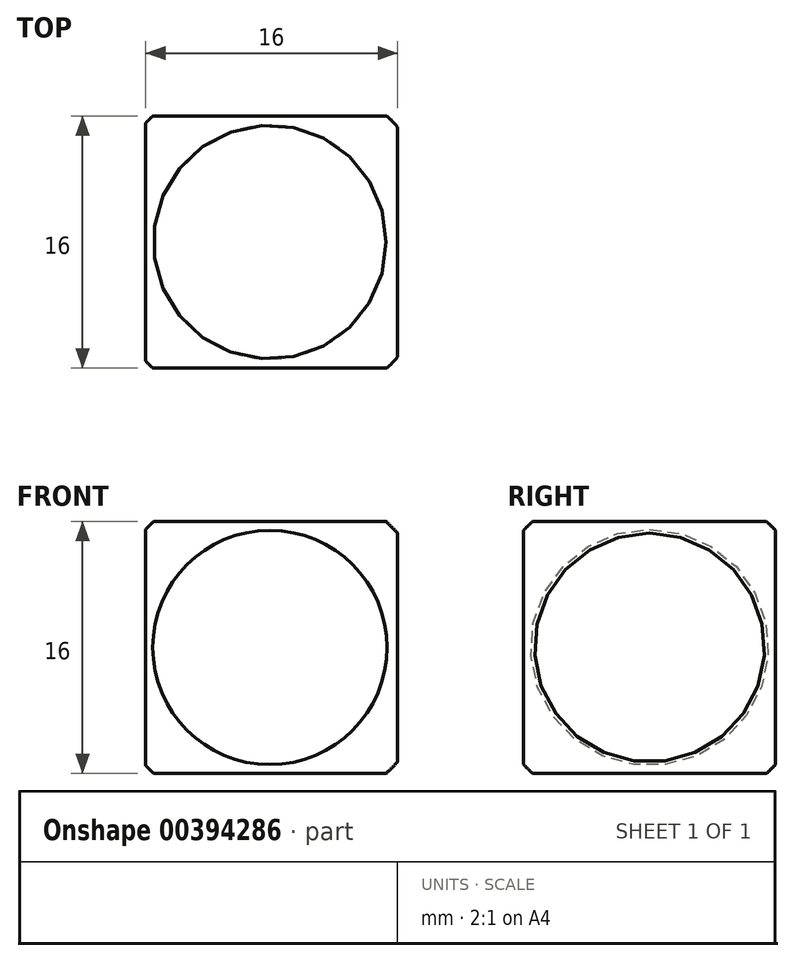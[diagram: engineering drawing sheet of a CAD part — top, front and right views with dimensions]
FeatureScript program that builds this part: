
annotation { "Feature Type Name" : "Feature", "Feature Type Description" : "" }
export const myFeature = defineFeature(function(context is Context, id is Id, definition is map)
    precondition{}
    {
        {
            var Q0;
            Q0=qCreatedBy(makeId("Top.planeOp"),FACE);
            var sketch = newSketch(context, id + "F0", { "sketchPlane" : qUnion([Q0])});
            skLineSegment(sketch, "E0.bottom", {"start": v(8, -8) * mm, "end": v(-8, -8) * mm});
            skLineSegment(sketch, "E0.top", {"start": v(8, 8) * mm, "end": v(-8, 8) * mm});
            skLineSegment(sketch, "E0.left", {"start": v(8, -8) * mm, "end": v(8, 8) * mm});
            skLineSegment(sketch, "E0.right", {"start": v(-8, -8) * mm, "end": v(-8, 8) * mm});
            skPoint(sketch, "E0.middle", {"position": v(0, 0) * mm});
            skSolve(sketch);
        }
        {
            var Q0;
            Q0 = qSketchRegion(id + "F0", true);
            extrude(context, id + "F1", {"entities" : qUnion([Q0]), "endBound" : BoundingType.SYMMETRIC, "depth" : 16 * mm});
        }
        {
            var Q0;
            Q0=qCreatedBy(makeId("Top.planeOp"),FACE);
            var sketch = newSketch(context, id + "F2", { "sketchPlane" : qUnion([Q0])});
            skArc(sketch, "E1", {"start": v(-0.11, 11) * mm, "mid": v(-11, 0) * mm, "end": v(-0.11, -11) * mm});
            skLineSegment(sketch, "E2", {"start": v(-0.11, 11) * mm, "end": v(-0.11, -11) * mm});
            skSolve(sketch);
        }
        {
            var Q0;
            Q0 = qSketchRegion(id + "F2", true);
            var Q1;
            Q1=sQuery(id+"F2.wireOp",EDGE,"E2");
            revolve(context, id + "F3", {"operationType" : NewBodyOperationType.INTERSECT, "entities" : qUnion([Q0]), "axis" : qUnion([Q1]), "revolveType" : RevolveType.FULL});
        }
    });
